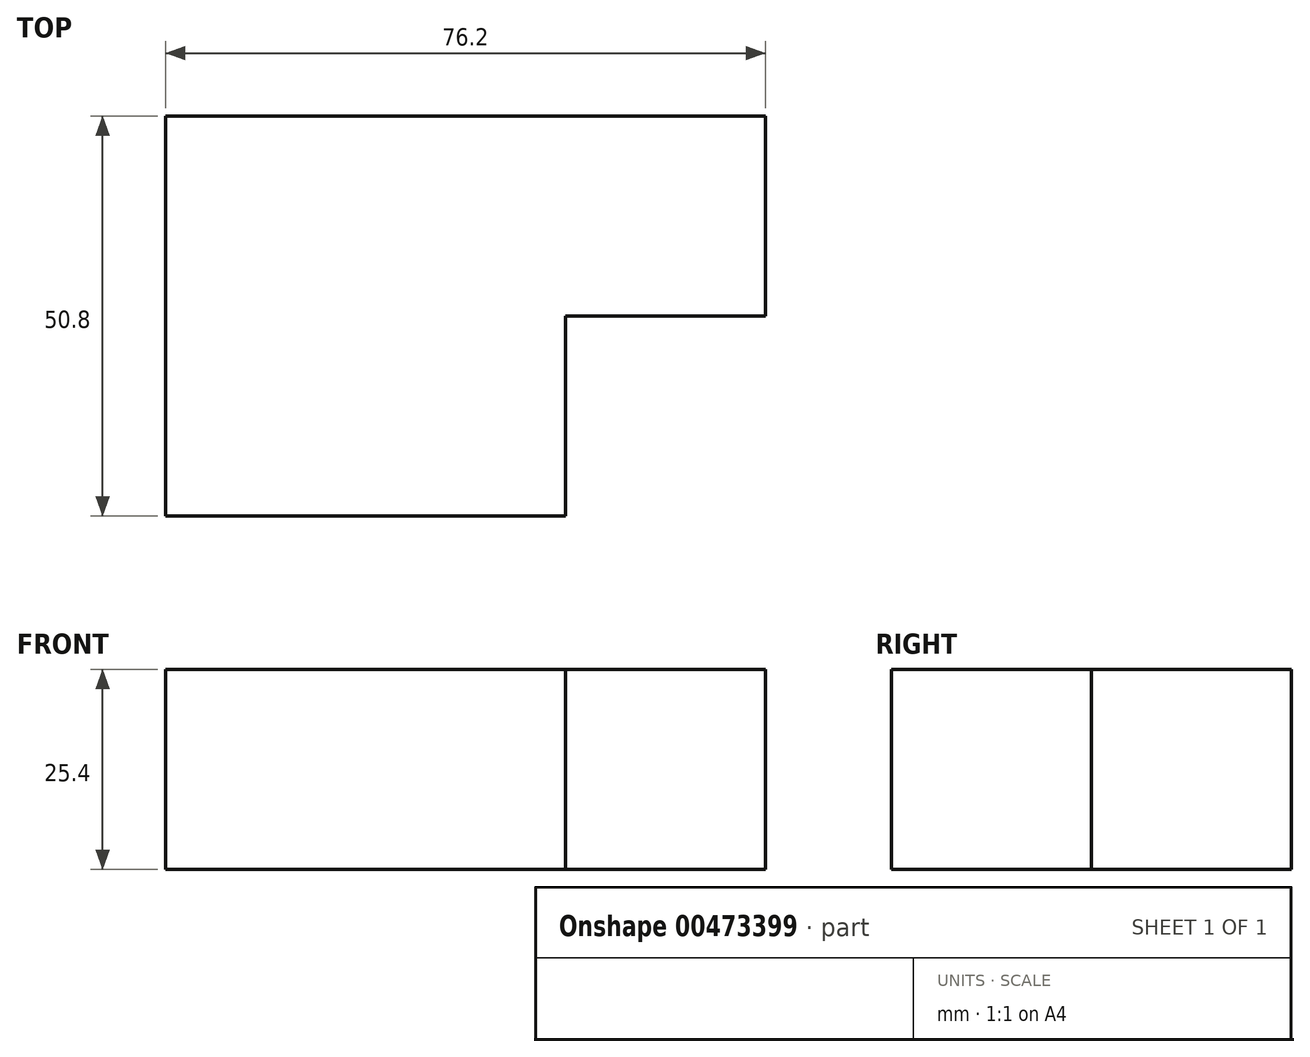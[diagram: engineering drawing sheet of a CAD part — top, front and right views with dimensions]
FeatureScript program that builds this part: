
annotation { "Feature Type Name" : "Feature", "Feature Type Description" : "" }
export const myFeature = defineFeature(function(context is Context, id is Id, definition is map)
    precondition{}
    {
        {
            var Q0;
            Q0=qCreatedBy(makeId("Top.planeOp"),FACE);
            var sketch = newSketch(context, id + "F0", { "sketchPlane" : qUnion([Q0])});
            skLineSegment(sketch, "E0", {"start": v(-50.8, -25.4) * mm, "end": v(-50.8, 25.4) * mm});
            skLineSegment(sketch, "E1", {"start": v(-50.8, 25.4) * mm, "end": v(25.4, 25.4) * mm});
            skLineSegment(sketch, "E2", {"start": v(25.4, 25.4) * mm, "end": v(25.4, 0) * mm});
            skLineSegment(sketch, "E3", {"start": v(25.4, 0) * mm, "end": v(0, 0) * mm});
            skLineSegment(sketch, "E4", {"start": v(0, 0) * mm, "end": v(0, -25.4) * mm});
            skLineSegment(sketch, "E5", {"start": v(0, -25.4) * mm, "end": v(-50.8, -25.4) * mm});
            skSolve(sketch);
        }
        {
            var Q0;
            Q0 = qSketchRegion(id + "F0", true);
            extrude(context, id + "F1", {"entities" : qUnion([Q0]), "depth" : 25.4 * mm});
        }
    });
